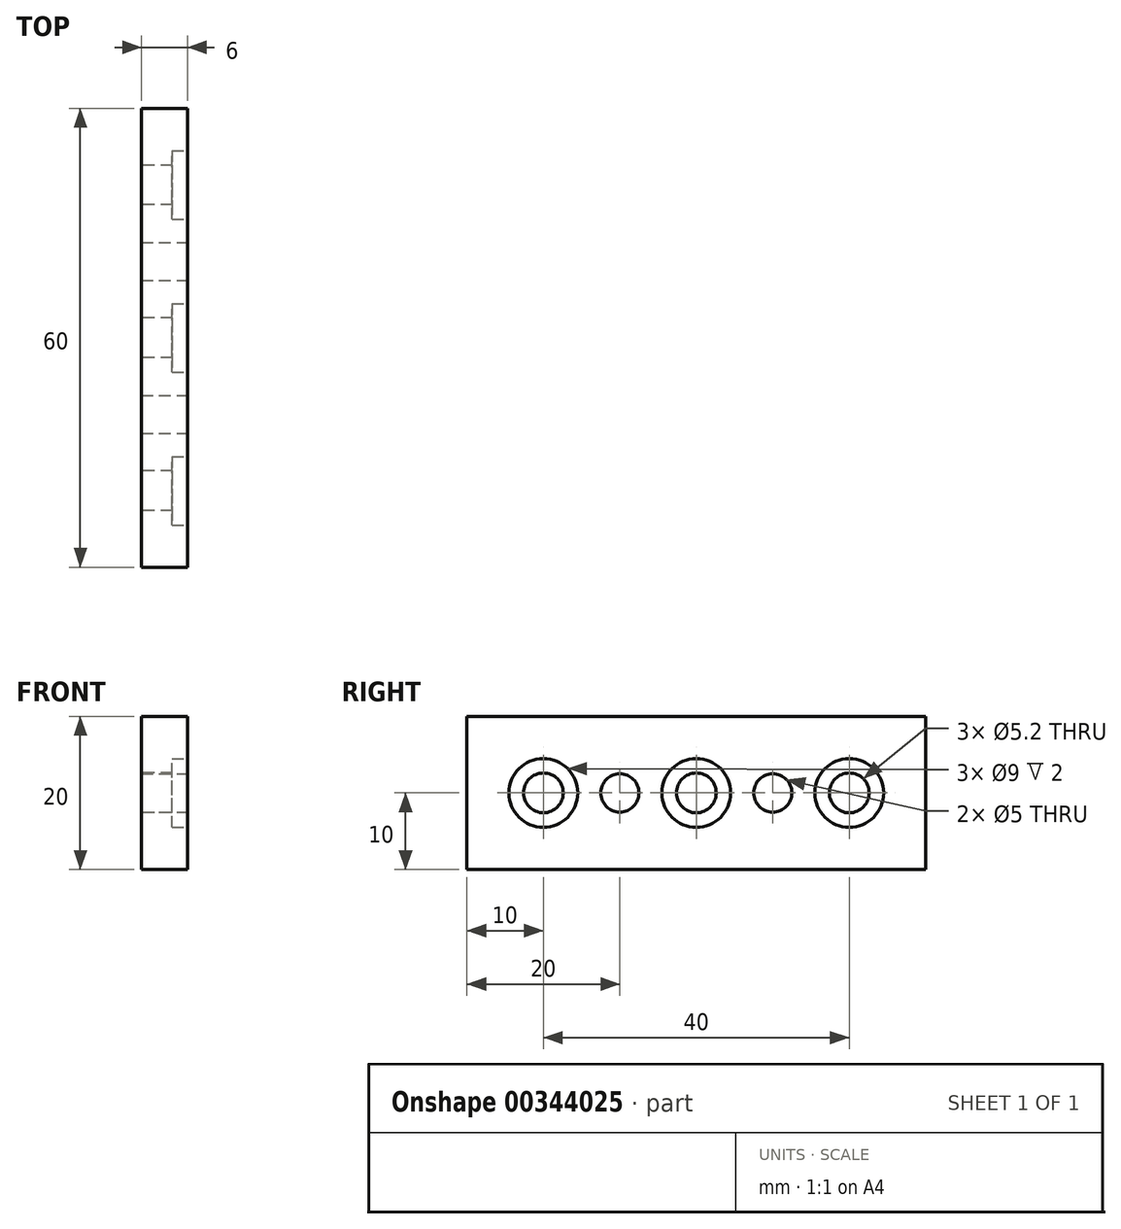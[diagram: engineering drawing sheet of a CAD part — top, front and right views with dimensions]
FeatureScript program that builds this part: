
annotation { "Feature Type Name" : "Feature", "Feature Type Description" : "" }
export const myFeature = defineFeature(function(context is Context, id is Id, definition is map)
    precondition{}
    {
        {
            var Q0;
            Q0=qCreatedBy(makeId("Right.planeOp"),FACE);
            var sketch = newSketch(context, id + "F0", { "sketchPlane" : qUnion([Q0])});
            skLineSegment(sketch, "E0.bottom", {"start": v(30, -10) * mm, "end": v(-30, -10) * mm});
            skLineSegment(sketch, "E0.top", {"start": v(30, 10) * mm, "end": v(-30, 10) * mm});
            skLineSegment(sketch, "E0.left", {"start": v(30, -10) * mm, "end": v(30, 10) * mm});
            skLineSegment(sketch, "E0.right", {"start": v(-30, -10) * mm, "end": v(-30, 10) * mm});
            skPoint(sketch, "E0.middle", {"position": v(0, 0) * mm});
            skCircle(sketch, "E1", {"center": v(-20, 0) * mm, "radius": 2.6 * mm});
            skCircle(sketch, "E2", {"center": v(20, 0) * mm, "radius": 2.6 * mm});
            skCircle(sketch, "E3", {"center": v(0, 0) * mm, "radius": 2.6 * mm});
            skSolve(sketch);
        }
        {
            var Q0;
            Q0=makeQuery(id+"F0.imprint","IMPRINT",FACE,{"disambiguationData":[TD([[makeQuery(id+"F0.imprint","IMPRINT",EDGE,{"derivedFrom":sQuery(id+"F0.wireOp",EDGE,"E0.bottom")}),-1.0]])]});
            extrude(context, id + "F1", {"entities" : qUnion([Q0]), "depth" : 6 * mm});
        }
        {
            var Q0;
            Q0=makeQuery(id+"F1.opExtrude","CAP_FACE",FACE,{"disambiguationData":[OSD([sQuery(id+"F0.wireOp",EDGE,"E0.bottom"),sQuery(id+"F0.wireOp",EDGE,"E0.top"),sQuery(id+"F0.wireOp",EDGE,"E0.left"),sQuery(id+"F0.wireOp",EDGE,"E0.right"),sQuery(id+"F0.wireOp",EDGE,"E1"),sQuery(id+"F0.wireOp",EDGE,"E2"),sQuery(id+"F0.wireOp",EDGE,"E3")])],"isStart":false});
            var sketch = newSketch(context, id + "F2", { "sketchPlane" : qUnion([Q0])});
            skCircle(sketch, "E4", {"center": v(-20, 0) * mm, "radius": 4.5 * mm});
            skCircle(sketch, "E5", {"center": v(0, 0) * mm, "radius": 4.5 * mm});
            skCircle(sketch, "E6", {"center": v(20, 0) * mm, "radius": 4.5 * mm});
            skSolve(sketch);
        }
        {
            var Q0;
            Q0=qSketchRegion(id+"F2",true);
            extrude(context, id + "F3", {"entities" : qUnion([Q0]), "operationType" : NewBodyOperationType.REMOVE, "oppositeDirection" : true, "depth" : 2 * mm});
        }
        {
            var Q0;
            Q0=makeQuery(id+"F1.opExtrude","CAP_FACE",FACE,{"disambiguationData":[OSD([sQuery(id+"F0.wireOp",EDGE,"E0.bottom"),sQuery(id+"F0.wireOp",EDGE,"E0.top"),sQuery(id+"F0.wireOp",EDGE,"E0.left"),sQuery(id+"F0.wireOp",EDGE,"E0.right"),sQuery(id+"F0.wireOp",EDGE,"E1"),sQuery(id+"F0.wireOp",EDGE,"E2"),sQuery(id+"F0.wireOp",EDGE,"E3")])],"isStart":false});
            var sketch = newSketch(context, id + "F4", { "sketchPlane" : qUnion([Q0])});
            skCircle(sketch, "E7", {"center": v(-10, 0) * mm, "radius": 2.5 * mm});
            skCircle(sketch, "E8", {"center": v(10, 0) * mm, "radius": 2.5 * mm});
            skSolve(sketch);
        }
        {
            var Q0;
            Q0 = qSketchRegion(id + "F4", true);
            extrude(context, id + "F5", {"entities" : qUnion([Q0]), "operationType" : NewBodyOperationType.REMOVE, "oppositeDirection" : true, "depth" : 25 * mm});
        }
    });
